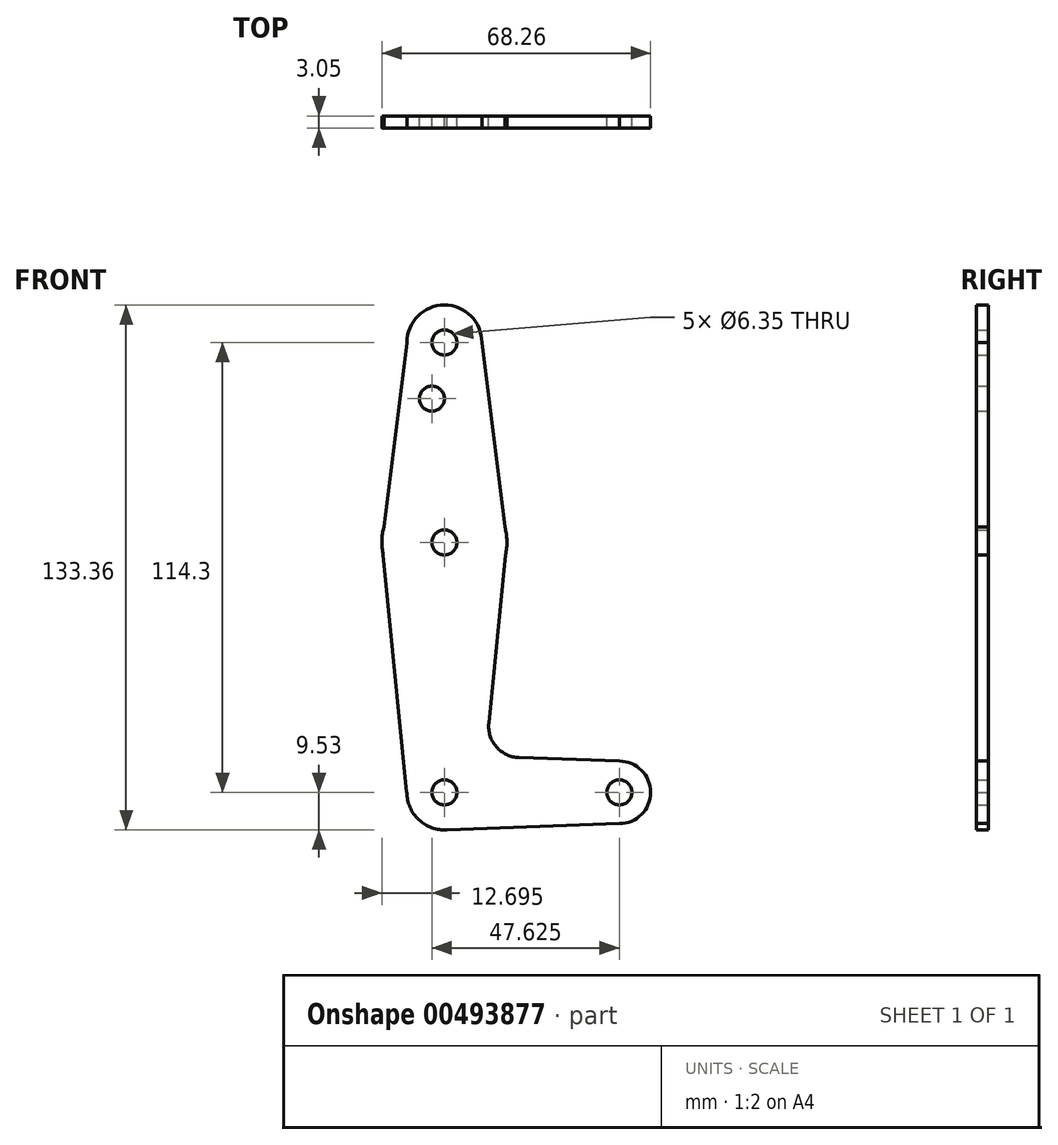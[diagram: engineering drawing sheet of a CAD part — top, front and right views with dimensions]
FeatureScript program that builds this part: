
annotation { "Feature Type Name" : "Feature", "Feature Type Description" : "" }
export const myFeature = defineFeature(function(context is Context, id is Id, definition is map)
    precondition{}
    {
        {
            var Q0;
            Q0=qCreatedBy(makeId("Front.planeOp"),FACE);
            var sketch = newSketch(context, id + "F0", { "sketchPlane" : qUnion([Q0])});
            skLineSegment(sketch, "E0", {"start": v(0, 114.3) * mm, "end": v(0, 0) * mm, "construction": true});
            skLineSegment(sketch, "E1", {"start": v(44.45, 0) * mm, "end": v(0, 0) * mm, "construction": true});
            skCircle(sketch, "E2", {"center": v(0, 63.5) * mm, "radius": 15.88 * mm});
            skCircle(sketch, "E3", {"center": v(0, 114.3) * mm, "radius": 9.53 * mm});
            skCircle(sketch, "E4", {"center": v(0, 0) * mm, "radius": 9.53 * mm});
            skCircle(sketch, "E5", {"center": v(44.45, 0) * mm, "radius": 7.94 * mm});
            skLineSegment(sketch, "E6", {"start": v(9.52, 114.3) * mm, "end": v(15.88, 63.5) * mm});
            skLineSegment(sketch, "E7", {"start": v(18.91, 8.85) * mm, "end": v(44.45, 7.94) * mm});
            skLineSegment(sketch, "E8", {"start": v(0, -9.53) * mm, "end": v(44.45, -7.94) * mm});
            skLineSegment(sketch, "E9", {"start": v(-9.53, 114.3) * mm, "end": v(-15.87, 63.5) * mm});
            skLineSegment(sketch, "E10", {"start": v(-15.87, 63.5) * mm, "end": v(-9.57, 0) * mm});
            skLineSegment(sketch, "E11", {"start": v(-9.57, 0) * mm, "end": v(9.53, 0) * mm});
            skLineSegment(sketch, "E12", {"start": v(11.28, 17.59) * mm, "end": v(15.88, 63.5) * mm});
            skCircle(sketch, "E13", {"center": v(0, 114.3) * mm, "radius": 3.18 * mm});
            skCircle(sketch, "E14", {"center": v(0, 63.5) * mm, "radius": 3.18 * mm});
            skCircle(sketch, "E15", {"center": v(0, 0) * mm, "radius": 3.18 * mm});
            skCircle(sketch, "E16", {"center": v(44.45, 0) * mm, "radius": 3.18 * mm});
            skCircle(sketch, "E17", {"center": v(-3.17, 100.03) * mm, "radius": 3.18 * mm});
            skArc(sketch, "E18.filletArc", {"start": v(11.28, 17.59) * mm, "mid": v(13.2, 11.57) * mm, "end": v(18.91, 8.85) * mm});
            skSolve(sketch);
        }
        {
            var Q0;
            Q0 = qSketchRegion(id + "F0", true);
            extrude(context, id + "F1", {"entities" : qUnion([Q0]), "depth" : 3.05 * mm});
        }
    });
